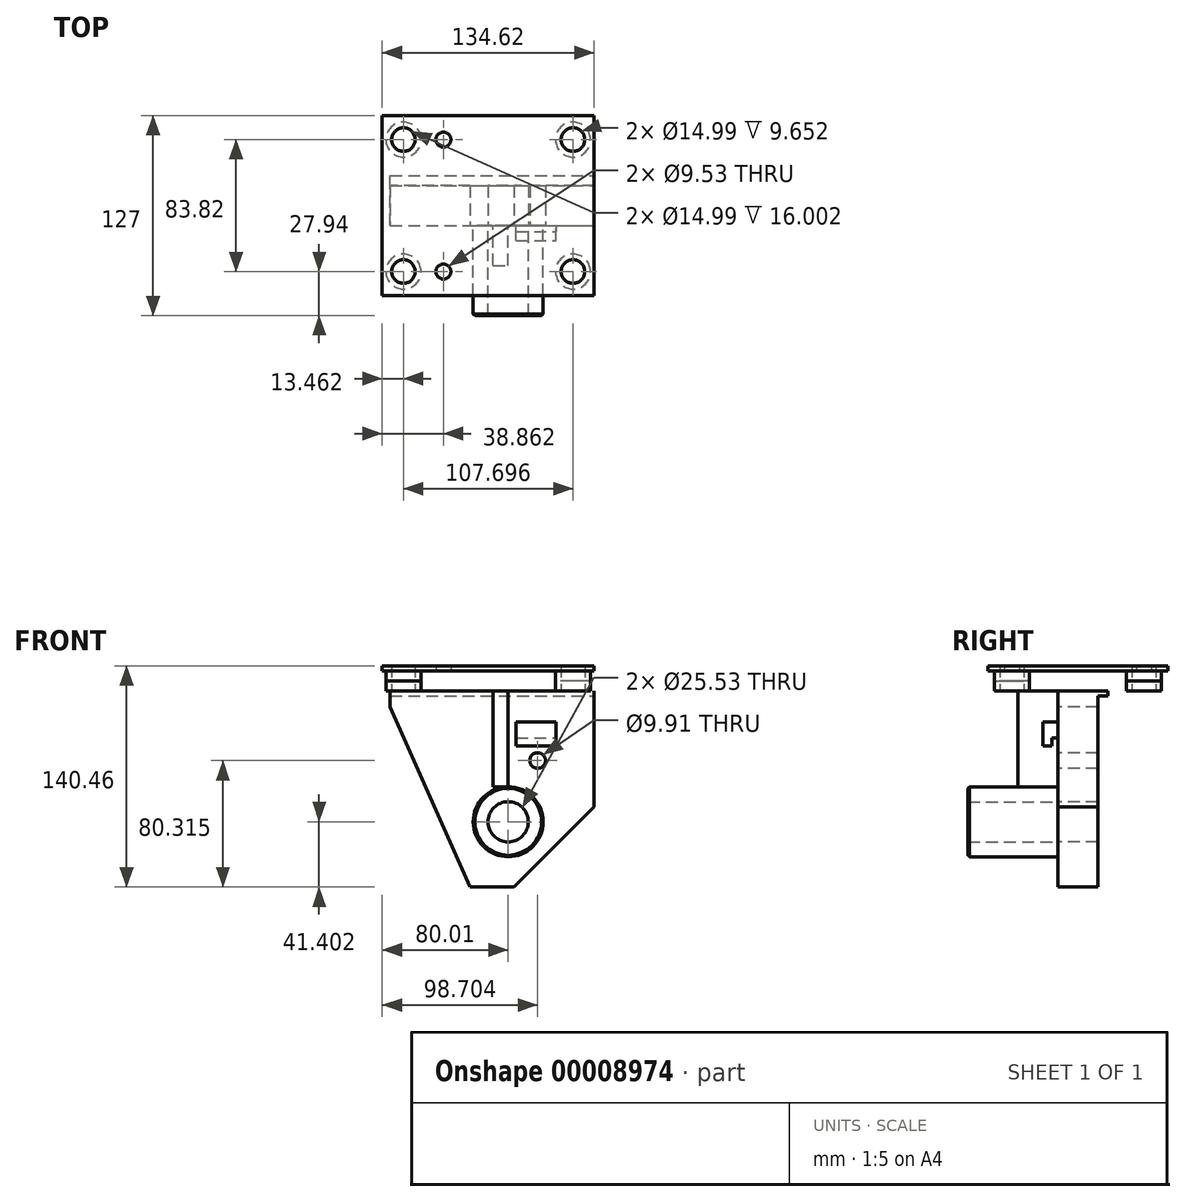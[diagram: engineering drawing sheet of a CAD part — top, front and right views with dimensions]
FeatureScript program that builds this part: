
annotation { "Feature Type Name" : "Feature", "Feature Type Description" : "" }
export const myFeature = defineFeature(function(context is Context, id is Id, definition is map)
    precondition{}
    {
        {
            var Q0;
            Q0=qCreatedBy(makeId("Top.planeOp"),FACE);
            var sketch = newSketch(context, id + "F0", { "sketchPlane" : qUnion([Q0])});
            skLineSegment(sketch, "E0.rect.bottom", {"start": v(-67.31, 57.15) * mm, "end": v(67.31, 57.15) * mm});
            skLineSegment(sketch, "E0.rect.top", {"start": v(-67.31, -57.15) * mm, "end": v(67.31, -57.15) * mm});
            skLineSegment(sketch, "E0.rect.left", {"start": v(-67.31, 57.15) * mm, "end": v(-67.31, -57.15) * mm});
            skLineSegment(sketch, "E0.rect.right", {"start": v(67.31, 57.15) * mm, "end": v(67.31, -57.15) * mm});
            skPoint(sketch, "E0.rect.middle", {"position": v(0, 0) * mm});
            skLineSegment(sketch, "E1.0", {"start": v(12.7, 57.15) * mm, "end": v(12.7, -57.15) * mm, "construction": true});
            skLineSegment(sketch, "E2.0", {"start": v(47.75, 57.15) * mm, "end": v(47.75, -57.15) * mm, "construction": true});
            skLineSegment(sketch, "E3.0", {"start": v(-53.85, 57.15) * mm, "end": v(-53.85, -57.15) * mm, "construction": true});
            skLineSegment(sketch, "E4", {"start": v(-67.31, 0) * mm, "end": v(67.31, 0) * mm, "construction": true});
            skLineSegment(sketch, "E5.0", {"start": v(-67.31, -41.91) * mm, "end": v(67.31, -41.91) * mm, "construction": true});
            skLineSegment(sketch, "E6.0.MirrorCS", {"start": v(-67.31, 41.91) * mm, "end": v(67.31, 41.91) * mm, "construction": true});
            skLineSegment(sketch, "E7.0", {"start": v(-28.45, 57.15) * mm, "end": v(-28.45, -57.15) * mm, "construction": true});
            skSolve(sketch);
        }
        {
            var Q0;
            Q0 = qSketchRegion(id + "F0", true);
            extrude(context, id + "F1", {"entities" : qUnion([Q0]), "depth" : 16 * mm});
        }
        {
            var Q0;
            Q0=makeQuery(id+"F0.imprint","IMPRINT",FACE,{"disambiguationData":[TD([[makeQuery(id+"F0.imprint","IMPRINT",EDGE,{"derivedFrom":sQuery(id+"F0.wireOp",EDGE,"E0.rect.bottom")}),-1.0]])]});
            var sketch = newSketch(context, id + "F2", { "sketchPlane" : qUnion([Q0])});
            skLineSegment(sketch, "E8.0", {"start": v(-67.31, -41.91) * mm, "end": v(67.31, -41.91) * mm, "construction": true});
            skLineSegment(sketch, "E9.0", {"start": v(-53.85, 57.15) * mm, "end": v(-53.85, -57.15) * mm, "construction": true});
            skLineSegment(sketch, "E10.0", {"start": v(-28.45, 57.15) * mm, "end": v(-28.45, -57.15) * mm, "construction": true});
            skLineSegment(sketch, "E11.0", {"start": v(-67.31, 41.91) * mm, "end": v(67.31, 41.91) * mm, "construction": true});
            skLineSegment(sketch, "E12.0", {"start": v(-67.31, 0) * mm, "end": v(67.31, 0) * mm, "construction": true});
            skCircle(sketch, "E13", {"center": v(-53.85, -41.91) * mm, "radius": 7.5 * mm});
            skCircle(sketch, "E14.0.MirrorC", {"center": v(-53.85, 41.91) * mm, "radius": 7.5 * mm});
            skLineSegment(sketch, "E15", {"start": v(0, -58.07) * mm, "end": v(0, 68.7) * mm, "construction": true});
            skCircle(sketch, "E16.0.MirrorC", {"center": v(53.85, 41.91) * mm, "radius": 7.5 * mm});
            skCircle(sketch, "E17.0.MirrorC", {"center": v(53.85, -41.91) * mm, "radius": 7.5 * mm});
            skCircle(sketch, "E18", {"center": v(-28.45, -41.91) * mm, "radius": 4.76 * mm});
            skCircle(sketch, "E19.0.MirrorC", {"center": v(-28.45, 41.91) * mm, "radius": 4.76 * mm});
            skSolve(sketch);
        }
        {
            var Q0;
            Q0 = qSketchRegion(id + "F2", true);
            extrude(context, id + "F3", {"entities" : qUnion([Q0]), "operationType" : NewBodyOperationType.REMOVE, "endBound" : BoundingType.THROUGH_ALL, "depth" : 25.4 * mm});
        }
        {
            var Q0;
            Q0=makeQuery(id+"F0.imprint","IMPRINT",FACE,{"disambiguationData":[TD([[makeQuery(id+"F0.imprint","IMPRINT",EDGE,{"derivedFrom":sQuery(id+"F0.wireOp",EDGE,"E0.rect.bottom")}),-1.0]])]});
            var sketch = newSketch(context, id + "F4", { "sketchPlane" : qUnion([Q0])});
            skCircle(sketch, "E20.0", {"center": v(-53.85, -41.91) * mm, "radius": 7.5 * mm, "construction": true});
            skCircle(sketch, "E21.0", {"center": v(53.85, -41.91) * mm, "radius": 7.5 * mm, "construction": true});
            skCircle(sketch, "E22.0", {"center": v(-53.85, 41.91) * mm, "radius": 7.5 * mm, "construction": true});
            skLineSegment(sketch, "E23.0", {"start": v(0, -58.07) * mm, "end": v(0, 68.7) * mm, "construction": true});
            skLineSegment(sketch, "E24.0", {"start": v(-67.31, 0) * mm, "end": v(67.31, 0) * mm, "construction": true});
            skCircle(sketch, "E25.0", {"center": v(53.85, 41.91) * mm, "radius": 7.5 * mm, "construction": true});
            skCircle(sketch, "E26", {"center": v(-53.85, -41.91) * mm, "radius": 11.11 * mm});
            skCircle(sketch, "E27.0.MirrorC", {"center": v(53.85, -41.91) * mm, "radius": 11.11 * mm});
            skCircle(sketch, "E28.0.MirrorC", {"center": v(53.85, 41.91) * mm, "radius": 11.11 * mm});
            skCircle(sketch, "E29.0.MirrorC", {"center": v(-53.85, 41.91) * mm, "radius": 11.11 * mm});
            skSolve(sketch);
        }
        {
            var Q0;
            Q0=makeQuery(id+"F4.imprint","IMPRINT",FACE,{"disambiguationData":[TD([[makeQuery(id+"F4.imprint","IMPRINT",EDGE,{"derivedFrom":sQuery(id+"F4.wireOp",EDGE,"E26")}),1.0]])]});
            var Q1;
            Q1=makeQuery(id+"F4.imprint","IMPRINT",FACE,{"disambiguationData":[TD([[makeQuery(id+"F4.imprint","IMPRINT",EDGE,{"derivedFrom":sQuery(id+"F4.wireOp",EDGE,"E27.0.MirrorC")}),-1.0]])]});
            var Q2;
            Q2=makeQuery(id+"F4.imprint","IMPRINT",FACE,{"disambiguationData":[TD([[makeQuery(id+"F4.imprint","IMPRINT",EDGE,{"derivedFrom":sQuery(id+"F4.wireOp",EDGE,"E28.0.MirrorC")}),1.0]])]});
            extrude(context, id + "F5", {"entities" : qUnion([Q0, Q1, Q2]), "operationType" : NewBodyOperationType.REMOVE, "depth" : 6.35 * mm});
        }
        {
            var Q0;
            Q0=makeQuery(id+"F4.imprint","IMPRINT",FACE,{"disambiguationData":[TD([[makeQuery(id+"F4.imprint","IMPRINT",EDGE,{"derivedFrom":sQuery(id+"F4.wireOp",EDGE,"E29.0.MirrorC")}),-1.0]])]});
            extrude(context, id + "F6", {"entities" : qUnion([Q0]), "operationType" : NewBodyOperationType.REMOVE, "depth" : 12.7 * mm});
        }
        {
            var Q0;
            Q0=makeQuery(id+"F4.imprint","IMPRINT",FACE,{"disambiguationData":[TD([[makeQuery(id+"F4.imprint","IMPRINT",EDGE,{"derivedFrom":sQuery(id+"F4.wireOp",EDGE,"E26")}),-1.0]])]});
            var sketch = newSketch(context, id + "F7", { "sketchPlane" : qUnion([Q0])});
            skLineSegment(sketch, "E30.0", {"start": v(-62.23, -12.7) * mm, "end": v(67.31, -12.7) * mm});
            skLineSegment(sketch, "E31.0", {"start": v(-62.23, 19.05) * mm, "end": v(67.31, 19.05) * mm});
            skLineSegment(sketch, "E32.0", {"start": v(60.96, 57.15) * mm, "end": v(60.96, -57.15) * mm, "construction": true});
            skLineSegment(sketch, "E33", {"start": v(67.31, -12.7) * mm, "end": v(67.31, 19.05) * mm});
            skLineSegment(sketch, "E34.0", {"start": v(-62.23, -12.7) * mm, "end": v(-62.23, 19.05) * mm});
            skSolve(sketch);
        }
        {
            var Q0;
            Q0 = qSketchRegion(id + "F7", true);
            extrude(context, id + "F8", {"entities" : qUnion([Q0]), "operationType" : NewBodyOperationType.ADD, "oppositeDirection" : true, "depth" : 124.46 * mm});
        }
        {
            var Q0;
            Q0=makeQuery(id+"F8.opExtrude","SWEPT_FACE",FACE,{"disambiguationData":[OSD([sQuery(id+"F7.wireOp",EDGE,"E31.0")])]});
            var sketch = newSketch(context, id + "F9", { "sketchPlane" : qUnion([Q0])});
            skLineSegment(sketch, "E35.0", {"start": v(67.31, -3.05) * mm, "end": v(-67.31, -3.05) * mm});
            skLineSegment(sketch, "E36.0", {"start": v(62.23, -124.46) * mm, "end": v(62.23, 0) * mm});
            skLineSegment(sketch, "E37.0", {"start": v(62.23, -124.46) * mm, "end": v(-67.31, -124.46) * mm});
            skLineSegment(sketch, "E38.0", {"start": v(-67.31, -124.46) * mm, "end": v(-67.31, 0) * mm});
            skSolve(sketch);
        }
        {
            var Q0;
            Q0 = qSketchRegion(id + "F9", true);
            extrude(context, id + "F10", {"entities" : qUnion([Q0]), "operationType" : NewBodyOperationType.REMOVE, "oppositeDirection" : true, "depth" : 6.38 * mm});
        }
        {
            var Q0;
            Q0=makeQuery(id+"F8.opExtrude","SWEPT_FACE",FACE,{"disambiguationData":[OSD([sQuery(id+"F7.wireOp",EDGE,"E30.0")])]});
            var sketch = newSketch(context, id + "F11", { "sketchPlane" : qUnion([Q0])});
            skLineSegment(sketch, "E39.0", {"start": v(-67.31, -10.16) * mm, "end": v(67.31, -10.16) * mm, "construction": true});
            skLineSegment(sketch, "E40.0", {"start": v(-11.43, -124.46) * mm, "end": v(-11.43, 0) * mm, "construction": true});
            skLineSegment(sketch, "E41.0", {"start": v(16.51, -124.46) * mm, "end": v(16.51, 0) * mm, "construction": true});
            skLineSegment(sketch, "E42.0", {"start": v(-62.23, -73.66) * mm, "end": v(67.31, -73.66) * mm, "construction": true});
            skLineSegment(sketch, "E43", {"start": v(-62.23, -10.16) * mm, "end": v(-11.43, -124.46) * mm});
            skLineSegment(sketch, "E44", {"start": v(16.51, -124.46) * mm, "end": v(67.31, -73.66) * mm});
            skLineSegment(sketch, "E45", {"start": v(67.31, -73.66) * mm, "end": v(67.31, -124.46) * mm});
            skLineSegment(sketch, "E46", {"start": v(67.31, -124.46) * mm, "end": v(16.51, -124.46) * mm});
            skLineSegment(sketch, "E47", {"start": v(-11.43, -124.46) * mm, "end": v(-62.23, -124.46) * mm});
            skLineSegment(sketch, "E48", {"start": v(-62.23, -124.46) * mm, "end": v(-62.23, -10.16) * mm});
            skSolve(sketch);
        }
        {
            var Q0;
            Q0 = qSketchRegion(id + "F11", true);
            extrude(context, id + "F12", {"entities" : qUnion([Q0]), "operationType" : NewBodyOperationType.REMOVE, "endBound" : BoundingType.THROUGH_ALL, "oppositeDirection" : true, "depth" : 25.4 * mm});
        }
        {
            var Q0;
            Q0=makeQuery(id+"F8.opExtrude","SWEPT_FACE",FACE,{"disambiguationData":[OSD([sQuery(id+"F7.wireOp",EDGE,"E30.0")])]});
            var sketch = newSketch(context, id + "F13", { "sketchPlane" : qUnion([Q0])});
            skLineSegment(sketch, "E49.0", {"start": v(67.31, -73.66) * mm, "end": v(67.31, 0) * mm, "construction": true});
            skLineSegment(sketch, "E50.0", {"start": v(12.7, -83.06) * mm, "end": v(12.7, -70.3) * mm, "construction": true});
            skLineSegment(sketch, "E51.0", {"start": v(-67.31, -83.06) * mm, "end": v(67.31, -83.06) * mm, "construction": true});
            skCircle(sketch, "E52", {"center": v(12.7, -83.06) * mm, "radius": 22.23 * mm});
            skLineSegment(sketch, "E53", {"start": v(12.7, -60.83) * mm, "end": v(12.7, 0) * mm});
            skCircle(sketch, "E54", {"center": v(12.7, -83.06) * mm, "radius": 12.76 * mm});
            skLineSegment(sketch, "E55.0", {"start": v(3.18, -60.83) * mm, "end": v(3.18, 0) * mm});
            skLineSegment(sketch, "E56", {"start": v(3.18, -60.83) * mm, "end": v(12.7, -60.83) * mm});
            skLineSegment(sketch, "E57", {"start": v(3.18, 0) * mm, "end": v(12.7, 0) * mm});
            skLineSegment(sketch, "E58.0", {"start": v(-67.31, -44.15) * mm, "end": v(67.31, -44.15) * mm, "construction": true});
            skLineSegment(sketch, "E59.0", {"start": v(31.4, -83.06) * mm, "end": v(31.4, -44.15) * mm, "construction": true});
            skCircle(sketch, "E60", {"center": v(31.4, -44.15) * mm, "radius": 4.95 * mm});
            skSolve(sketch);
        }
        {
            var Q0;
            Q0=makeQuery(id+"F13.imprint","IMPRINT",FACE,{"disambiguationData":[TD([[makeQuery(id+"F13.imprint","IMPRINT",EDGE,{"derivedFrom":sQuery(id+"F13.wireOp",EDGE,"E53")}),1.0]])]});
            extrude(context, id + "F14", {"entities" : qUnion([Q0]), "operationType" : NewBodyOperationType.ADD, "depth" : 25.4 * mm});
        }
        {
            var Q0;
            Q0=makeQuery(id+"F13.imprint","IMPRINT",FACE,{"disambiguationData":[TD([[makeQuery(id+"F13.imprint","IMPRINT",EDGE,{"derivedFrom":sQuery(id+"F13.wireOp",EDGE,"E52")}),1.0]])]});
            extrude(context, id + "F15", {"entities" : qUnion([Q0]), "depth" : 57.15 * mm});
        }
        {
            var Q0;
            Q0=makeQuery(id+"F13.imprint","IMPRINT",FACE,{"disambiguationData":[TD([[makeQuery(id+"F13.imprint","IMPRINT",EDGE,{"derivedFrom":sQuery(id+"F13.wireOp",EDGE,"E60")}),1.0]])]});
            extrude(context, id + "F16", {"entities" : qUnion([Q0]), "operationType" : NewBodyOperationType.REMOVE, "endBound" : BoundingType.THROUGH_ALL, "oppositeDirection" : true, "depth" : 25.4 * mm});
        }
        {
            var Q0;
            Q0=makeQuery(id+"F13.imprint","IMPRINT",FACE,{"disambiguationData":[TD([[makeQuery(id+"F13.imprint","IMPRINT",EDGE,{"derivedFrom":sQuery(id+"F13.wireOp",EDGE,"E52")}),-1.0]])]});
            var sketch = newSketch(context, id + "F17", { "sketchPlane" : qUnion([Q0])});
            skCircle(sketch, "E61.0", {"center": v(12.7, -83.06) * mm, "radius": 12.76 * mm});
            skSolve(sketch);
        }
        {
            var Q0;
            Q0 = qSketchRegion(id + "F17", true);
            extrude(context, id + "F18", {"entities" : qUnion([Q0]), "operationType" : NewBodyOperationType.REMOVE, "endBound" : BoundingType.THROUGH_ALL, "oppositeDirection" : true, "depth" : 25.4 * mm});
        }
        {
            var Q0;
            Q0=makeQuery(id+"F15.opExtrude","CAP_EDGE",EDGE,{"disambiguationData":[OSD([sQuery(id+"F13.wireOp",EDGE,"E52")])],"isStart":false});
            chamfer(context, id + "F19", {"entities" : qUnion([Q0]), "width" : 1.02 * mm, "tangentPropagation" : true});
        }
        {
            var Q0;
            Q0=makeQuery(id+"F8.opExtrude","SWEPT_FACE",FACE,{"disambiguationData":[OSD([sQuery(id+"F7.wireOp",EDGE,"E30.0")])]});
            var sketch = newSketch(context, id + "F20", { "sketchPlane" : qUnion([Q0])});
            skCircle(sketch, "E62.0.1", {"center": v(12.7, -83.06) * mm, "radius": 22.23 * mm});
            skLineSegment(sketch, "E62.0.2", {"start": v(12.7, -60.83) * mm, "end": v(3.18, -60.83) * mm});
            skLineSegment(sketch, "E62.0.4", {"start": v(3.18, 0) * mm, "end": v(-62.23, 0) * mm});
            skLineSegment(sketch, "E62.0.10", {"start": v(67.31, 0) * mm, "end": v(12.7, 0) * mm});
            skLineSegment(sketch, "E63.0", {"start": v(17.78, -34.8) * mm, "end": v(17.78, -19.56) * mm});
            skLineSegment(sketch, "E64.0", {"start": v(43.18, -34.8) * mm, "end": v(43.18, -19.56) * mm});
            skLineSegment(sketch, "E65.0", {"start": v(17.78, -34.8) * mm, "end": v(43.18, -34.8) * mm});
            skLineSegment(sketch, "E66.trimOffspring", {"start": v(17.78, -19.56) * mm, "end": v(43.18, -19.56) * mm});
            skPoint(sketch, "E62.0.8.end.orphan", {"position": v(67.31, -73.66) * mm});
            skPoint(sketch, "E62.0.5.end.orphan", {"position": v(-62.23, -10.16) * mm});
            skPoint(sketch, "E62.0.7.end.orphan", {"position": v(16.51, -124.46) * mm});
            skPoint(sketch, "E62.0.7.start.orphan", {"position": v(-11.43, -124.46) * mm});
            skSolve(sketch);
        }
        {
            var Q0;
            Q0=makeQuery(id+"F20.imprint","IMPRINT",FACE,{"disambiguationData":[TD([[makeQuery(id+"F20.imprint","IMPRINT",EDGE,{"derivedFrom":sQuery(id+"F20.wireOp",EDGE,"E63.0")}),-1.0]])]});
            extrude(context, id + "F21", {"entities" : qUnion([Q0]), "operationType" : NewBodyOperationType.ADD, "depth" : 9.52 * mm});
        }
        {
            var Q0;
            Q0=makeQuery(id+"F21.opExtrude","SWEPT_FACE",FACE,{"disambiguationData":[OSD([sQuery(id+"F20.wireOp",EDGE,"E64.0")])]});
            var sketch = newSketch(context, id + "F22", { "sketchPlane" : qUnion([Q0])});
            skLineSegment(sketch, "E67.bottom", {"start": v(-12.7, -34.8) * mm, "end": v(-16.51, -34.8) * mm});
            skLineSegment(sketch, "E67.top", {"start": v(-12.7, -29.72) * mm, "end": v(-16.51, -29.72) * mm});
            skLineSegment(sketch, "E67.left", {"start": v(-12.7, -34.8) * mm, "end": v(-12.7, -29.72) * mm});
            skLineSegment(sketch, "E67.right", {"start": v(-16.51, -34.8) * mm, "end": v(-16.51, -29.72) * mm});
            skSolve(sketch);
        }
        {
            var Q0;
            Q0 = qSketchRegion(id + "F22", true);
            var Q1;
            Q1=makeQuery(id+"F14.opExtrude","SWEPT_FACE",FACE,{"disambiguationData":[OSD([sQuery(id+"F13.wireOp",EDGE,"E53")])]});
            extrude(context, id + "F23", {"entities" : qUnion([Q0]), "operationType" : NewBodyOperationType.REMOVE, "endBound" : BoundingType.UP_TO_SURFACE, "oppositeDirection" : true, "endBoundEntityFace" : qUnion([Q1]), "depth" : 25.4 * mm});
        }
    });
